# Revit family: Velos
name_source: partatom
category: Lighting Fixtures
revit_build: Autodesk Revit MEP 2012 (Build: 20110916_2132(x64)
units: mm (PartAtom-declared; Revit-internal decimal feet)

## types (2) — shared parameters
Apparent Load = 5 VA
Body Material = Eaton – (Body, PSU - polycarbonate, RAL9016)
Circuit Watts = 3 W
Emergency = Yes
Height = 224 mm  [stored 0.734908 ft]
IP Rating = IP20
LOR = 1
Lamp = LED strip
Legend panel Material = Eaton – (Legend panel, Polycarbonate, Clear)
Length = 346 mm  [stored 1.13517 ft]
Manufacturer = EATON
Model = VELOS
Power Factor = 0.7
Special Considerations 1 = Legends sold separate
Special Considerations 2 = Can be supplied to operate with CBU/CEAG System
Special Considerations 3 = Can be supplied to operate with our Easicheck system
Special Considerations 4 = Can be supplied recessed, Wall mounted, Rope Suspension, Rod Suspension and Lateral mounted (Accessaries sold separate)
URL = http://www.cooper-ls.com
Voltage = 230 V
Wattage Comments = 3.2W LED
Width = 69 mm  [stored 0.226378 ft]

## per-type parameters (varying)
| type | Ceiling Mount | Default Elevation | Description | Wall Mount | Weight |
| O-ESC-3H + O-ESP-IU | Yes | 0 mm  [stored 0 ft] | Ceiling mounted LED exit sign. Legends sold separate | No | 0.6 |
| O-ESC-3H + O-ESA-FLEX + O-ESP-IU | No | 2200 mm | Wall mounted LED exit sign. Legends sold separate | Yes | 0.65 |

note: column(s) folded — value = type name in every type: Part No.

note: [stored X ft] marks values corroborated as IEEE doubles in the binary element streams (Revit-internal decimal feet)

## geometry (parser evidence)
native form markers: Blend x3, Sweep x8
no freeform markers — native parametric forms only
